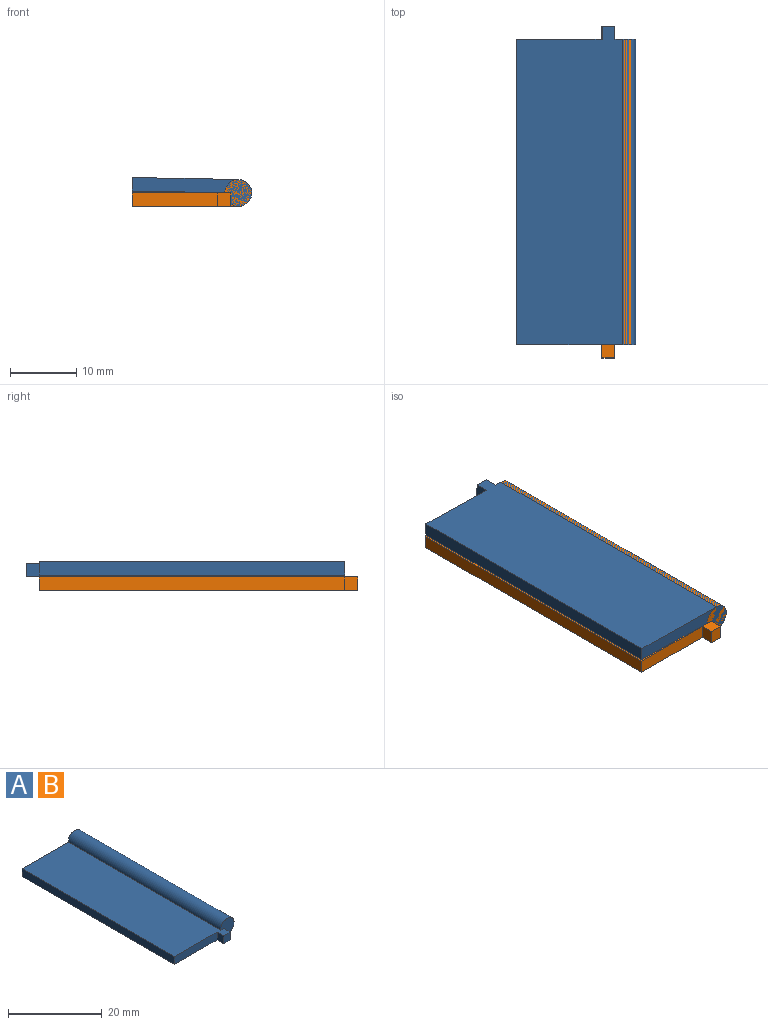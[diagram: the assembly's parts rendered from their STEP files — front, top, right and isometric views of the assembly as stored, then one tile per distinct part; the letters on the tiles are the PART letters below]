
ASSEMBLY  parts=2 mates=1
PART A: 10 faces, bbox 18x48x4.1 mm
  f0: plane 4.06x4.06mm, normal (0,-1,0), area 12.1mm2, adj f2,f3,f4,f8
  f1: plane 46x2.03mm, normal (-1,0,0), area 93.5mm2, adj f2,f4,f5,f6
  f2: plane 48x15.97mm, normal (0,0,-1), area 738.4mm2, adj f0,f1,f3,f5,f6,f7,f8,f9
  f3: cylinder r=2.03mm len=46mm, axis (0,1,0), area 440.5mm2, adj f0,f2,f4,f6
  f4: plane 48x14.83mm, normal (0,0,1), area 644.9mm2, adj f0,f1,f3,f5,f6,f7,f8,f9
  f5: plane 12.88x2.03mm, normal (0,-1,0), area 26.2mm2, adj f1,f2,f4,f7
  f6: plane 18x4.06mm, normal (0,1,0), area 42.2mm2, adj f1,f2,f3,f4
  f7: plane 2.03x2mm, normal (-1,0,0), area 4.1mm2, adj f2,f4,f5,f9
  f8: plane 2.03x2mm, normal (1,0,0), area 4.1mm2, adj f0,f2,f4,f9
  f9: plane 2.03x1.94mm, normal (0,-1,0), area 3.9mm2, adj f2,f4,f7,f8
PART B: same geometry as A
PLACE A rot(axis=(1,0,-0.01),180deg) t=(23.19,-22.32,7.1)mm
PLACE B t=(23.15,23.68,2.75)mm fixed
MATE revolute A.f3 <-> B.f3  axis (0,1,0) through (39.12,23.68,4.78)mm
